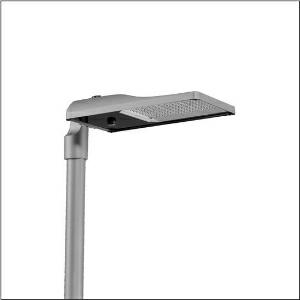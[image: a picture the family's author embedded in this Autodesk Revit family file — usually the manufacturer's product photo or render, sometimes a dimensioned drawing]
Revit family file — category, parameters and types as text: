
# Revit family: streetlight_sl_31_maxi___st0_5a_5xh8b31t08sa_315f
name_source: partatom
category: Lighting Fixtures
units: mm (PartAtom-declared; Revit-internal decimal feet)

## family parameters
Cut with Voids When Loaded = No
Host = Face
Light Source = No
Part Type = Normal
Room Calculation Point = No
Round Connector Dimension = Use Diameter
Shared = No

## types (1)
- --- (1 x LED, 28310 lm, 211.4 W, 3000K)
    Apparent Load = 211 VA
    CIE Flux Codes = 41 75 97 100 100
    Color Rendering = 70
    Color Temperature = 3000K
    Default Elevation = 1800 mm
    Description = Streetlight SL 31 maxi D4i, Desk-Remote mast luminaire for post-top, side-entry; light control with lens of PMMA; light distribution: ST0.5a, direct asymmetric distribution, for standard-compliant lighting for roads and squares; LED: luminous flux: 28.310lm, light colour: 730, colour temperature: 3000K; luminous efficacy: 133,9lm/W; control: pre-setting: logarithmic dimming characteristic, flexible luminous flux parameterisation, time-dependent luminous flux control, constant luminous flux control, power reduction, intelligent temperature release in ECG and LED module, overheat protection; luminaire housing, of diecast aluminium, Siteco® metallic grey (DB 702S), corrosivity category C5 high according to DIN EN ISO 12944; cover of toughened safety glass, transparent, opened without tools; mast flange of diecast aluminium, Siteco® metallic grey (DB 702S), spigot size: 76/60mm, mast flange included unmounted; with cable H07RN-F 2x 1.5mm², cable length: 14,5m, connection cable pre-assembled; mains connection: 220..240V, AC, 50/60Hz; power consumption (at start of service life): 211,4W / (at end of service life): 238W / (with reduced operation 50%): 88,1W; protection rating (complete): IP66; insulation class (complete): insulation class II (safety insulation); impact resistance: IK09; certification: CE, ENEC, ENEC+, VDE, UKCA, ZD4i; permissible operating ambient temperature for outdoor applications: -40..+50°C; packaging unit: 1 piece

Light Distribution: ST0.5a
    Height = 79 mm
    Lamp = 1 x LED
    Lamp Light Flux = 28310 lm
    Lamp Power = 211.4 W
    Lamp count = 1
    Length = 657 mm
    Luminous efficacy = 134 lm/W
    Manufacturer = Siteco
    ModVariant = No
    Model = 5XH8B31T08SA
    Number of Poles = 1
    OnlyDefault = Yes
    Power Factor = 1
    Product Name = Streetlight SL 31 maxi | ST0.5a
    Product group = mast luminaire | pylon top
    ProductGroupID = 6100
    Protection Class = Protection class II
    Protection Degree = IP 66
    RLX_Detail_Level = 1
    RLX_Emergency_Light_Flux = 0 lm
    RLX_Emergency_Type = 0
    RLX_Emergency_Type_DB = No
    RlxData = <blob elided: 58241 chars, md5=f323eff5>
    Socket = socket
    Standby Power = 0 W
    System Light Flux = 28311 lm
    System Power = 211 W
    Type Comments = factory setting: luminous flux: 100 % | dim-lin: 254 | 727 mA
    Type Image = l_1300303.jpg
    URL = http://relux.com
    VarID = @adj_060415
    Voltage = 0 V
    Weight = 0.00 kg
    Width = 362 mm

## geometry (parser evidence)
native form markers: Blend x4, Sweep x12
no freeform markers — native parametric forms only
